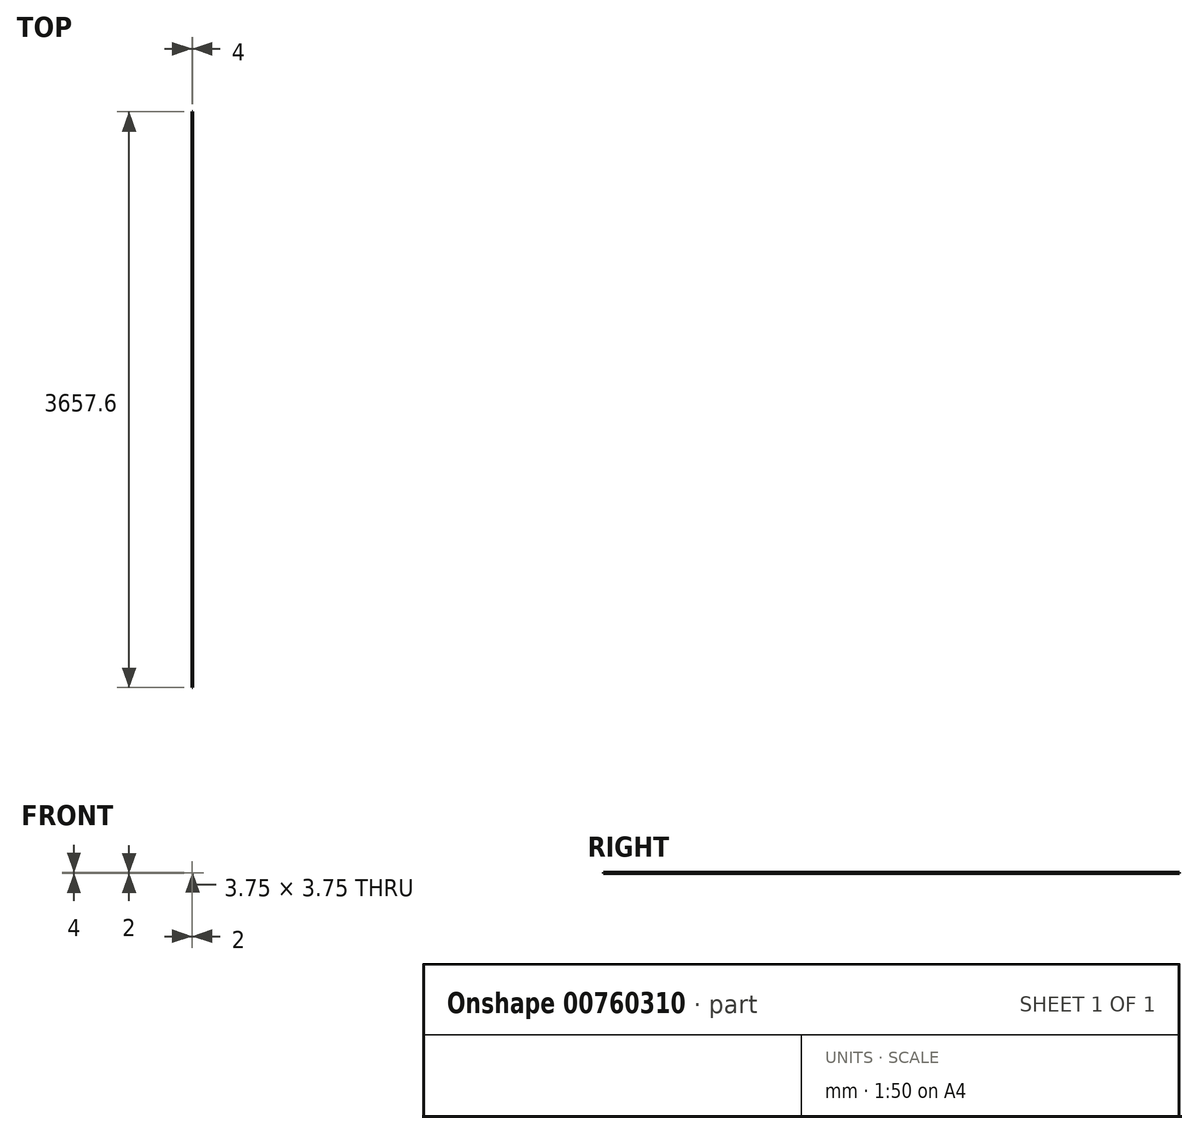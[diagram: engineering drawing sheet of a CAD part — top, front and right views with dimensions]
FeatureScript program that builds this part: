
annotation { "Feature Type Name" : "Feature", "Feature Type Description" : "" }
export const myFeature = defineFeature(function(context is Context, id is Id, definition is map)
    precondition{}
    {
        {
            var Q0;
            Q0=qCreatedBy(makeId("Front.planeOp"),FACE);
            var sketch = newSketch(context, id + "F0", { "sketchPlane" : qUnion([Q0])});
            skLineSegment(sketch, "E0.bottom", {"start": v(2, 2) * mm, "end": v(-2, 2) * mm});
            skLineSegment(sketch, "E0.top", {"start": v(2, -2) * mm, "end": v(-2, -2) * mm});
            skLineSegment(sketch, "E0.left", {"start": v(2, 2) * mm, "end": v(2, -2) * mm});
            skLineSegment(sketch, "E0.right", {"start": v(-2, 2) * mm, "end": v(-2, -2) * mm});
            skPoint(sketch, "E0.middle", {"position": v(0, 0) * mm});
            skLineSegment(sketch, "E1.bottom", {"start": v(1.87, 1.88) * mm, "end": v(-1.88, 1.87) * mm});
            skLineSegment(sketch, "E1.top", {"start": v(1.88, -1.87) * mm, "end": v(-1.87, -1.88) * mm});
            skLineSegment(sketch, "E1.left", {"start": v(1.87, 1.88) * mm, "end": v(1.88, -1.87) * mm});
            skLineSegment(sketch, "E1.right", {"start": v(-1.88, 1.87) * mm, "end": v(-1.87, -1.88) * mm});
            skSolve(sketch);
        }
        {
            var Q0;
            Q0=makeQuery(id+"F0.imprint","IMPRINT",FACE,{"disambiguationData":[TD([[makeQuery(id+"F0.imprint","IMPRINT",EDGE,{"derivedFrom":sQuery(id+"F0.wireOp",EDGE,"E0.bottom")}),1.0]])]});
            extrude(context, id + "F1", {"entities" : qUnion([Q0]), "depth" : 3657.6 * mm, "offsetDistance" : 25 * mm});
        }
    });
